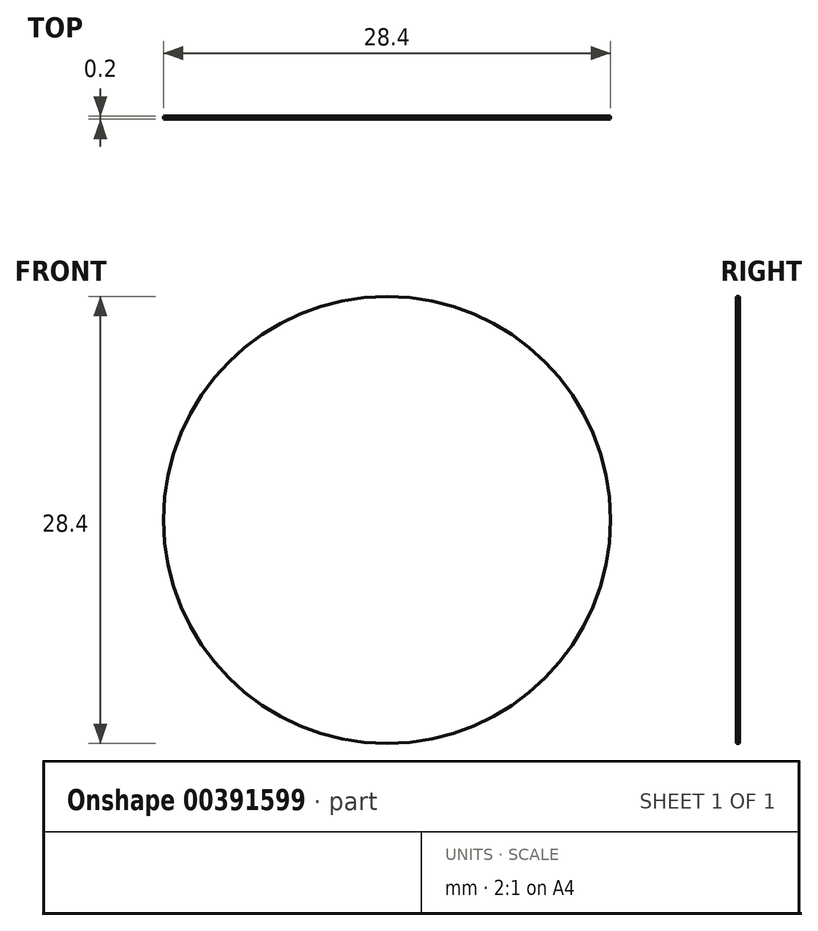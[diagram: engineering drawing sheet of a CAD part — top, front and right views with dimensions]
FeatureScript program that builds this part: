
annotation { "Feature Type Name" : "Feature", "Feature Type Description" : "" }
export const myFeature = defineFeature(function(context is Context, id is Id, definition is map)
    precondition{}
    {
        {
            var Q0;
            Q0=qCreatedBy(makeId("Front.planeOp"),FACE);
            var sketch = newSketch(context, id + "F0", { "sketchPlane" : qUnion([Q0])});
            skCircle(sketch, "E0", {"center": v(0, 0) * mm, "radius": 9 * mm, "construction": true});
            skCircle(sketch, "E1", {"center": v(0, 0) * mm, "radius": 10.5 * mm, "construction": true});
            skLineSegment(sketch, "E2", {"start": v(0, 9) * mm, "end": v(0.75, 9) * mm, "construction": true});
            skLineSegment(sketch, "E3", {"start": v(0.75, 9) * mm, "end": v(0.75, 13.5) * mm, "construction": true});
            skLineSegment(sketch, "E4", {"start": v(0.75, 13.5) * mm, "end": v(0, 13.5) * mm, "construction": true});
            skLineSegment(sketch, "E5", {"start": v(0, 13.5) * mm, "end": v(-0.75, 13.5) * mm, "construction": true});
            skLineSegment(sketch, "E6", {"start": v(-0.75, 13.5) * mm, "end": v(-0.75, 9) * mm, "construction": true});
            skLineSegment(sketch, "E7", {"start": v(-0.75, 9) * mm, "end": v(0, 9) * mm, "construction": true});
            skLineSegment(sketch, "E8.1.0", {"start": v(-3.85, 8.17) * mm, "end": v(-6.1, 12.07) * mm});
            skLineSegment(sketch, "E8.1.1", {"start": v(-7.4, 11.32) * mm, "end": v(-5.15, 7.42) * mm});
            skLineSegment(sketch, "E8.1.2", {"start": v(-5.15, 7.42) * mm, "end": v(-4.5, 7.8) * mm});
            skLineSegment(sketch, "E8.1.3", {"start": v(-4.5, 7.8) * mm, "end": v(-3.85, 8.17) * mm});
            skLineSegment(sketch, "E8.1.4", {"start": v(-6.1, 12.07) * mm, "end": v(-6.75, 11.7) * mm});
            skLineSegment(sketch, "E8.1.5", {"start": v(-6.75, 11.7) * mm, "end": v(-7.4, 11.32) * mm});
            skLineSegment(sketch, "E8.2.0", {"start": v(-7.42, 5.15) * mm, "end": v(-11.32, 7.4) * mm});
            skLineSegment(sketch, "E8.2.1", {"start": v(-12.07, 6.1) * mm, "end": v(-8.17, 3.85) * mm});
            skLineSegment(sketch, "E8.2.2", {"start": v(-8.17, 3.85) * mm, "end": v(-7.8, 4.5) * mm});
            skLineSegment(sketch, "E8.2.3", {"start": v(-7.8, 4.5) * mm, "end": v(-7.42, 5.15) * mm});
            skLineSegment(sketch, "E8.2.4", {"start": v(-11.32, 7.4) * mm, "end": v(-11.7, 6.75) * mm});
            skLineSegment(sketch, "E8.2.5", {"start": v(-11.7, 6.75) * mm, "end": v(-12.07, 6.1) * mm});
            skLineSegment(sketch, "E8.3.0", {"start": v(-9, 0.75) * mm, "end": v(-13.5, 0.75) * mm, "construction": true});
            skLineSegment(sketch, "E8.3.1", {"start": v(-13.5, -0.75) * mm, "end": v(-9, -0.75) * mm, "construction": true});
            skLineSegment(sketch, "E8.3.2", {"start": v(-9, -0.75) * mm, "end": v(-9, 0) * mm, "construction": true});
            skLineSegment(sketch, "E8.3.3", {"start": v(-9, 0) * mm, "end": v(-9, 0.75) * mm, "construction": true});
            skLineSegment(sketch, "E8.3.4", {"start": v(-13.5, 0.75) * mm, "end": v(-13.5, 0) * mm, "construction": true});
            skLineSegment(sketch, "E8.3.5", {"start": v(-13.5, 0) * mm, "end": v(-13.5, -0.75) * mm, "construction": true});
            skLineSegment(sketch, "E8.4.0", {"start": v(-8.17, -3.85) * mm, "end": v(-12.07, -6.1) * mm});
            skLineSegment(sketch, "E8.4.1", {"start": v(-11.32, -7.4) * mm, "end": v(-7.42, -5.15) * mm});
            skLineSegment(sketch, "E8.4.2", {"start": v(-7.42, -5.15) * mm, "end": v(-7.8, -4.5) * mm});
            skLineSegment(sketch, "E8.4.3", {"start": v(-7.8, -4.5) * mm, "end": v(-8.17, -3.85) * mm});
            skLineSegment(sketch, "E8.4.4", {"start": v(-12.07, -6.1) * mm, "end": v(-11.7, -6.75) * mm});
            skLineSegment(sketch, "E8.4.5", {"start": v(-11.7, -6.75) * mm, "end": v(-11.32, -7.4) * mm});
            skLineSegment(sketch, "E8.5.0", {"start": v(-5.15, -7.42) * mm, "end": v(-7.4, -11.32) * mm});
            skLineSegment(sketch, "E8.5.1", {"start": v(-6.1, -12.07) * mm, "end": v(-3.85, -8.17) * mm});
            skLineSegment(sketch, "E8.5.2", {"start": v(-3.85, -8.17) * mm, "end": v(-4.5, -7.8) * mm});
            skLineSegment(sketch, "E8.5.3", {"start": v(-4.5, -7.8) * mm, "end": v(-5.15, -7.42) * mm});
            skLineSegment(sketch, "E8.5.4", {"start": v(-7.4, -11.32) * mm, "end": v(-6.75, -11.7) * mm});
            skLineSegment(sketch, "E8.5.5", {"start": v(-6.75, -11.7) * mm, "end": v(-6.1, -12.07) * mm});
            skLineSegment(sketch, "E8.6.0", {"start": v(-0.75, -9) * mm, "end": v(-0.75, -13.5) * mm, "construction": true});
            skLineSegment(sketch, "E8.6.1", {"start": v(0.75, -13.5) * mm, "end": v(0.75, -9) * mm, "construction": true});
            skLineSegment(sketch, "E8.6.2", {"start": v(0.75, -9) * mm, "end": v(0, -9) * mm, "construction": true});
            skLineSegment(sketch, "E8.6.3", {"start": v(0, -9) * mm, "end": v(-0.75, -9) * mm, "construction": true});
            skLineSegment(sketch, "E8.6.4", {"start": v(-0.75, -13.5) * mm, "end": v(0, -13.5) * mm, "construction": true});
            skLineSegment(sketch, "E8.6.5", {"start": v(0, -13.5) * mm, "end": v(0.75, -13.5) * mm, "construction": true});
            skLineSegment(sketch, "E8.7.0", {"start": v(3.85, -8.17) * mm, "end": v(6.1, -12.07) * mm});
            skLineSegment(sketch, "E8.7.1", {"start": v(7.4, -11.32) * mm, "end": v(5.15, -7.42) * mm});
            skLineSegment(sketch, "E8.7.2", {"start": v(5.15, -7.42) * mm, "end": v(4.5, -7.8) * mm});
            skLineSegment(sketch, "E8.7.3", {"start": v(4.5, -7.8) * mm, "end": v(3.85, -8.17) * mm});
            skLineSegment(sketch, "E8.7.4", {"start": v(6.1, -12.07) * mm, "end": v(6.75, -11.7) * mm});
            skLineSegment(sketch, "E8.7.5", {"start": v(6.75, -11.7) * mm, "end": v(7.4, -11.32) * mm});
            skLineSegment(sketch, "E8.8.0", {"start": v(7.42, -5.15) * mm, "end": v(11.32, -7.4) * mm});
            skLineSegment(sketch, "E8.8.1", {"start": v(12.07, -6.1) * mm, "end": v(8.17, -3.85) * mm});
            skLineSegment(sketch, "E8.8.2", {"start": v(8.17, -3.85) * mm, "end": v(7.8, -4.5) * mm});
            skLineSegment(sketch, "E8.8.3", {"start": v(7.8, -4.5) * mm, "end": v(7.42, -5.15) * mm});
            skLineSegment(sketch, "E8.8.4", {"start": v(11.32, -7.4) * mm, "end": v(11.7, -6.75) * mm});
            skLineSegment(sketch, "E8.8.5", {"start": v(11.7, -6.75) * mm, "end": v(12.07, -6.1) * mm});
            skLineSegment(sketch, "E8.9.0", {"start": v(9, -0.75) * mm, "end": v(13.5, -0.75) * mm, "construction": true});
            skLineSegment(sketch, "E8.9.1", {"start": v(13.5, 0.75) * mm, "end": v(9, 0.75) * mm, "construction": true});
            skLineSegment(sketch, "E8.9.2", {"start": v(9, 0.75) * mm, "end": v(9, 0) * mm, "construction": true});
            skLineSegment(sketch, "E8.9.3", {"start": v(9, 0) * mm, "end": v(9, -0.75) * mm, "construction": true});
            skLineSegment(sketch, "E8.9.4", {"start": v(13.5, -0.75) * mm, "end": v(13.5, 0) * mm, "construction": true});
            skLineSegment(sketch, "E8.9.5", {"start": v(13.5, 0) * mm, "end": v(13.5, 0.75) * mm, "construction": true});
            skLineSegment(sketch, "E8.10.0", {"start": v(8.17, 3.85) * mm, "end": v(12.07, 6.1) * mm});
            skLineSegment(sketch, "E8.10.1", {"start": v(11.32, 7.4) * mm, "end": v(7.42, 5.15) * mm});
            skLineSegment(sketch, "E8.10.2", {"start": v(7.42, 5.15) * mm, "end": v(7.8, 4.5) * mm});
            skLineSegment(sketch, "E8.10.3", {"start": v(7.8, 4.5) * mm, "end": v(8.17, 3.85) * mm});
            skLineSegment(sketch, "E8.10.4", {"start": v(12.07, 6.1) * mm, "end": v(11.7, 6.75) * mm});
            skLineSegment(sketch, "E8.10.5", {"start": v(11.7, 6.75) * mm, "end": v(11.32, 7.4) * mm});
            skLineSegment(sketch, "E8.11.0", {"start": v(5.15, 7.42) * mm, "end": v(7.4, 11.32) * mm});
            skLineSegment(sketch, "E8.11.1", {"start": v(6.1, 12.07) * mm, "end": v(3.85, 8.17) * mm});
            skLineSegment(sketch, "E8.11.2", {"start": v(3.85, 8.17) * mm, "end": v(4.5, 7.8) * mm});
            skLineSegment(sketch, "E8.11.3", {"start": v(4.5, 7.8) * mm, "end": v(5.15, 7.42) * mm});
            skLineSegment(sketch, "E8.11.4", {"start": v(7.4, 11.32) * mm, "end": v(6.75, 11.7) * mm});
            skLineSegment(sketch, "E8.11.5", {"start": v(6.75, 11.7) * mm, "end": v(6.1, 12.07) * mm});
            skCircle(sketch, "E9", {"center": v(0, 0) * mm, "radius": 13.5 * mm, "construction": true});
            skSolve(sketch);
        }
        {
            var Q0;
            Q0=qCreatedBy(makeId("Front.planeOp"),FACE);
            var sketch = newSketch(context, id + "F1", { "sketchPlane" : qUnion([Q0])});
            skText(sketch, "E10", { "text": "12", "fontName": "AllertaStencil-Regular.ttf"});
            skText(sketch, "E11", { "text": "6", "fontName": "AllertaStencil-Regular.ttf"});
            skText(sketch, "E12", { "text": "9", "fontName": "AllertaStencil-Regular.ttf"});
            skPoint(sketch, "E13", {"position": v(-13.5, 0) * mm});
            skText(sketch, "E14", { "text": "3", "fontName": "AllertaStencil-Regular.ttf"});
            skCircle(sketch, "E15", {"center": v(0, 0) * mm, "radius": 13.5 * mm, "construction": true});
            skCircle(sketch, "E16", {"center": v(0, 0) * mm, "radius": 10 * mm, "construction": true});
            skLineSegment(sketch, "E17", {"start": v(0, 0) * mm, "end": v(0, 13.5) * mm, "construction": true});
            skLineSegment(sketch, "E18.1.0", {"start": v(0, 0) * mm, "end": v(-13.5, 0) * mm, "construction": true});
            skLineSegment(sketch, "E18.2.0", {"start": v(0, 0) * mm, "end": v(0, -13.5) * mm, "construction": true});
            skLineSegment(sketch, "E18.3.0", {"start": v(0, 0) * mm, "end": v(13.5, 0) * mm, "construction": true});
            skPoint(sketch, "E19", {"position": v(13.5, 0) * mm});
            const initialGuessF1  = {"E10": [-0.00246, 0.01, 1, 0, 0.0035], "E11": [-0.00153, -0.0135, 1, 0, 0.0035], "E12": [-0.0135, -0.00175, 1, 0, 0.0035], "E14": [0.01076, -0.00175, 1, 0, 0.0035]};
            skSetInitialGuess(sketch, initialGuessF1);
            skSolve(sketch);
        }
        {
            var Q0;
            Q0=qCreatedBy(makeId("Front.planeOp"),FACE);
            var sketch = newSketch(context, id + "F2", { "sketchPlane" : qUnion([Q0])});
            skCircle(sketch, "E20", {"center": v(0, 0) * mm, "radius": 14.2 * mm});
            skSolve(sketch);
        }
        {
            var Q0;
            Q0=qCreatedBy(makeId("Front.planeOp"),FACE);
            var sketch = newSketch(context, id + "F3", { "sketchPlane" : qUnion([Q0])});
            skLineSegment(sketch, "E21", {"start": v(-1.79, 9.56) * mm, "end": v(1.79, 9.56) * mm});
            skLineSegment(sketch, "E22", {"start": v(1.79, 9.56) * mm, "end": v(0, 6.46) * mm});
            skLineSegment(sketch, "E23", {"start": v(0, 6.46) * mm, "end": v(-1.79, 9.56) * mm});
            skSolve(sketch);
        }
        {
            var Q0;
            Q0=qCreatedBy(makeId("Front.planeOp"),FACE);
            var sketch = newSketch(context, id + "F4", { "sketchPlane" : qUnion([Q0])});
            skLineSegment(sketch, "E24.bottom", {"start": v(-9.63, -0.91) * mm, "end": v(-6.95, -0.91) * mm});
            skLineSegment(sketch, "E24.top", {"start": v(-9.63, 0.91) * mm, "end": v(-6.95, 0.91) * mm});
            skLineSegment(sketch, "E24.left", {"start": v(-9.63, -0.91) * mm, "end": v(-9.63, 0.91) * mm});
            skLineSegment(sketch, "E24.right", {"start": v(-6.95, -0.91) * mm, "end": v(-6.95, 0.91) * mm});
            skPoint(sketch, "E25", {"position": v(-6.95, 0) * mm});
            skLineSegment(sketch, "E26.1.0", {"start": v(-0.91, -9.63) * mm, "end": v(-0.91, -6.95) * mm});
            skLineSegment(sketch, "E26.1.1", {"start": v(0.91, -9.63) * mm, "end": v(-0.91, -9.63) * mm});
            skLineSegment(sketch, "E26.1.2", {"start": v(0.91, -6.95) * mm, "end": v(-0.91, -6.95) * mm});
            skPoint(sketch, "E26.1.3", {"position": v(0, -6.95) * mm});
            skLineSegment(sketch, "E26.1.4", {"start": v(0.91, -9.63) * mm, "end": v(0.91, -6.95) * mm});
            skLineSegment(sketch, "E26.2.0", {"start": v(9.63, -0.91) * mm, "end": v(6.95, -0.91) * mm});
            skLineSegment(sketch, "E26.2.1", {"start": v(9.63, 0.91) * mm, "end": v(9.63, -0.91) * mm});
            skLineSegment(sketch, "E26.2.2", {"start": v(6.95, 0.91) * mm, "end": v(6.95, -0.91) * mm});
            skPoint(sketch, "E26.2.3", {"position": v(6.95, 0) * mm});
            skLineSegment(sketch, "E26.2.4", {"start": v(9.63, 0.91) * mm, "end": v(6.95, 0.91) * mm});
            skLineSegment(sketch, "E26.3.0", {"start": v(0.91, 9.63) * mm, "end": v(0.91, 6.95) * mm, "construction": true});
            skLineSegment(sketch, "E26.3.1", {"start": v(-0.91, 9.63) * mm, "end": v(0.91, 9.63) * mm, "construction": true});
            skLineSegment(sketch, "E26.3.2", {"start": v(-0.91, 6.95) * mm, "end": v(0.91, 6.95) * mm, "construction": true});
            skPoint(sketch, "E26.3.3", {"position": v(0, 6.95) * mm});
            skLineSegment(sketch, "E26.3.4", {"start": v(-0.91, 9.63) * mm, "end": v(-0.91, 6.95) * mm, "construction": true});
            skPoint(sketch, "E26.center", {"position": v(0, 0) * mm});
            skSolve(sketch);
        }
        {
            var Q0;
            Q0=qCreatedBy(makeId("Front.planeOp"),FACE);
            var sketch = newSketch(context, id + "F5", { "sketchPlane" : qUnion([Q0])});
            skCircle(sketch, "E27", {"center": v(0, 0) * mm, "radius": 7.75 * mm, "construction": true});
            skCircle(sketch, "E28", {"center": v(0, 7.75) * mm, "radius": 0.75 * mm, "construction": true});
            skCircle(sketch, "E29.1.0", {"center": v(-3.87, 6.71) * mm, "radius": 0.75 * mm});
            skCircle(sketch, "E29.2.0", {"center": v(-6.71, 3.88) * mm, "radius": 0.75 * mm});
            skCircle(sketch, "E29.3.0", {"center": v(-7.75, 0) * mm, "radius": 0.75 * mm});
            skCircle(sketch, "E29.4.0", {"center": v(-6.71, -3.87) * mm, "radius": 0.75 * mm});
            skCircle(sketch, "E29.5.0", {"center": v(-3.88, -6.71) * mm, "radius": 0.75 * mm});
            skCircle(sketch, "E29.6.0", {"center": v(0, -7.75) * mm, "radius": 0.75 * mm});
            skCircle(sketch, "E29.7.0", {"center": v(3.87, -6.71) * mm, "radius": 0.75 * mm});
            skCircle(sketch, "E29.8.0", {"center": v(6.71, -3.88) * mm, "radius": 0.75 * mm});
            skCircle(sketch, "E29.9.0", {"center": v(7.75, 0) * mm, "radius": 0.75 * mm});
            skCircle(sketch, "E29.10.0", {"center": v(6.71, 3.87) * mm, "radius": 0.75 * mm});
            skCircle(sketch, "E29.11.0", {"center": v(3.87, 6.71) * mm, "radius": 0.75 * mm});
            skSolve(sketch);
        }
        {
            var Q0;
            Q0=qSketchRegion(id+"F2",true);
            extrude(context, id + "F6", {"entities" : qUnion([Q0]), "depth" : 0.2 * mm});
        }
    });
